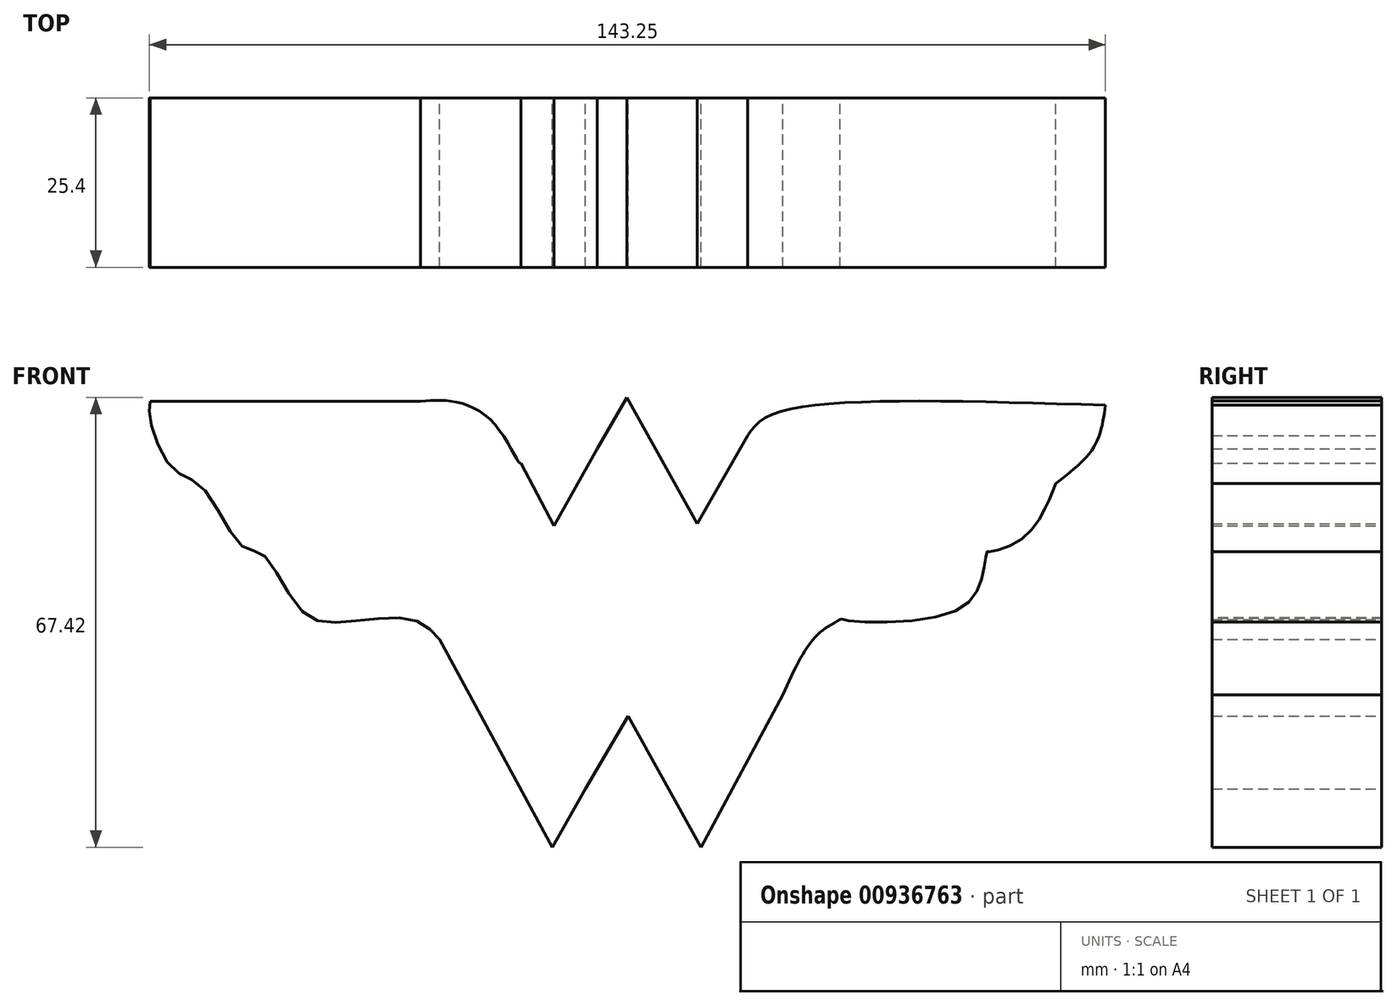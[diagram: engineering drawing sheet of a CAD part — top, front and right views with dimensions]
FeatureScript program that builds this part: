
annotation { "Feature Type Name" : "Feature", "Feature Type Description" : "" }
export const myFeature = defineFeature(function(context is Context, id is Id, definition is map)
    precondition{}
    {
        {
            var Q0;
            Q0=qCreatedBy(makeId("Front.planeOp"),FACE);
            var sketch = newSketch(context, id + "F0", { "sketchPlane" : qUnion([Q0])});
            skLineSegment(sketch, "E0", {"start": v(-70.5, 34.84) * mm, "end": v(-29.98, 34.84) * mm});
            skFitSpline(sketch, "E1", {"points": [v(-29.98, 34.84) * mm, v(-25.2, 34.84) * mm, v(-18.97, 31.51) * mm, v(-15.23, 25.7) * mm, v(-14.93, 25.55) * mm], "startDerivative": vector(16.98, 1.49) * mm, "endDerivative": vector(3.64, -0.33) * mm});
            skLineSegment(sketch, "E2", {"start": v(-14.93, 25.55) * mm, "end": v(-9.98, 16.17) * mm});
            skLineSegment(sketch, "E3", {"start": v(-9.98, 16.17) * mm, "end": v(-3.5, 27.75) * mm});
            skLineSegment(sketch, "E4", {"start": v(-3.5, 27.75) * mm, "end": v(0.92, 35.43) * mm});
            skLineSegment(sketch, "E5", {"start": v(0.92, 35.43) * mm, "end": v(11.47, 16.51) * mm});
            skLineSegment(sketch, "E6", {"start": v(11.47, 16.51) * mm, "end": v(19.03, 29.73) * mm});
            skFitSpline(sketch, "E7", {"points": [v(19.03, 29.73) * mm, v(21.36, 32.18) * mm, v(31.64, 34.5) * mm, v(72.63, 34.26) * mm], "startDerivative": vector(11.56, 16.37) * mm, "endDerivative": vector(84.13, -2.69) * mm});
            skFitSpline(sketch, "E8", {"points": [v(72.63, 34.26) * mm, v(70.91, 28.02) * mm, v(65.16, 22.51) * mm], "startDerivative": vector(-1.88, -13.8) * mm, "endDerivative": vector(-12.86, -9.76) * mm});
            skFitSpline(sketch, "E9", {"points": [v(65.16, 22.51) * mm, v(63.83, 19.3) * mm, v(59.76, 13.99) * mm, v(55.07, 12.3) * mm, v(54.9, 12.3) * mm, v(54.36, 9.38) * mm, v(49.58, 3.19) * mm, v(33.14, 2.17) * mm, v(33.05, 2.26) * mm, v(32.87, 2.17) * mm], "startDerivative": vector(-9.91, -26.17) * mm, "endDerivative": vector(-8.28, -5.4) * mm});
            skFitSpline(sketch, "E10", {"points": [v(32.87, 2.17) * mm, v(28.85, -0.84) * mm, v(24.28, -9.17) * mm], "startDerivative": vector(-9.91, -5.61) * mm, "endDerivative": vector(-7.4, -16.5) * mm});
            skLineSegment(sketch, "E11", {"start": v(24.28, -9.17) * mm, "end": v(12.02, -31.99) * mm});
            skLineSegment(sketch, "E12", {"start": v(12.02, -31.99) * mm, "end": v(1.1, -12.36) * mm});
            skLineSegment(sketch, "E13", {"start": v(-10.24, -31.99) * mm, "end": v(-27.14, -0.84) * mm});
            skFitSpline(sketch, "E14", {"points": [v(-27.14, -0.84) * mm, v(-30.87, 2.02) * mm, v(-40.4, 1.88) * mm, v(-47.57, 3.2) * mm, v(-53.53, 11.82) * mm, v(-56.71, 13.15) * mm, v(-62.8, 22.03) * mm, v(-67.18, 24.81) * mm, v(-70.5, 32.1) * mm, v(-70.5, 34.84) * mm], "startDerivative": vector(-32.22, 37.22) * mm, "endDerivative": vector(4.46, 31.3) * mm});
            skLineSegment(sketch, "E15", {"start": v(1.1, -12.36) * mm, "end": v(-5.29, -23.24) * mm});
            skLineSegment(sketch, "E16", {"start": v(-5.29, -23.24) * mm, "end": v(-10.24, -31.99) * mm});
            skSolve(sketch);
        }
        {
            var Q0;
            Q0 = qSketchRegion(id + "F0", true);
            extrude(context, id + "F1", {"entities" : qUnion([Q0]), "depth" : 25.4 * mm, "offsetDistance" : 25.4 * mm});
        }
    });
